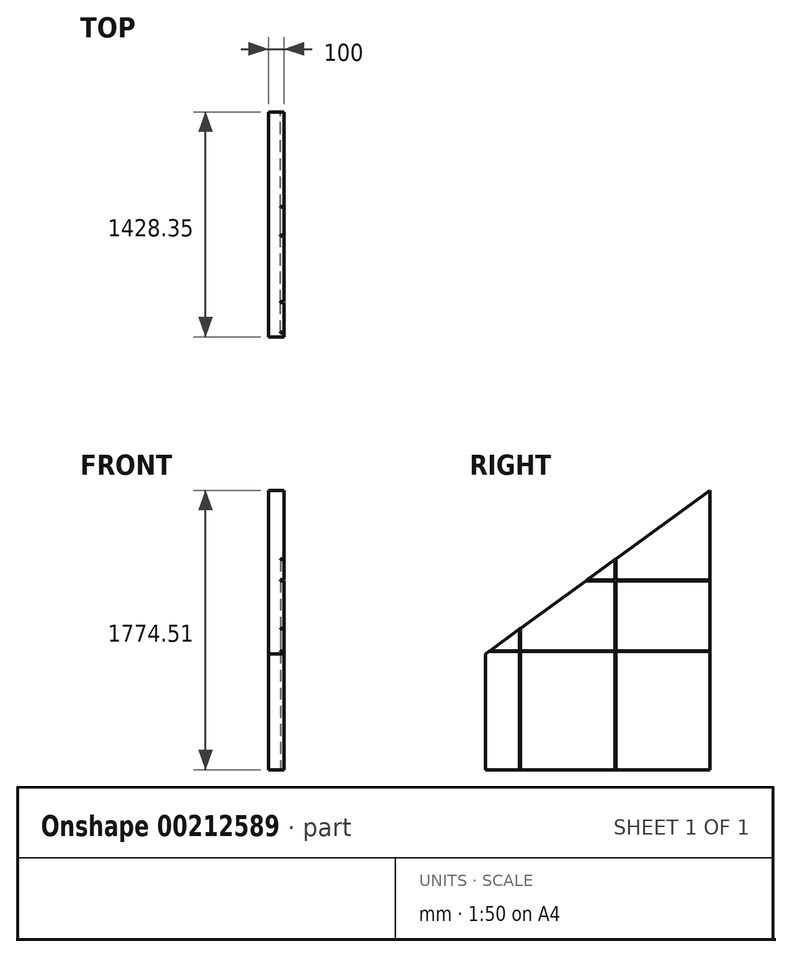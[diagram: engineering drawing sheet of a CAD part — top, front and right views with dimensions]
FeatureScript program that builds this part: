
annotation { "Feature Type Name" : "Feature", "Feature Type Description" : "" }
export const myFeature = defineFeature(function(context is Context, id is Id, definition is map)
    precondition{}
    {
        {
            var Q0;
            Q0=qCreatedBy(makeId("Right.planeOp"),FACE);
            var sketch = newSketch(context, id + "F0", { "sketchPlane" : qUnion([Q0])});
            skLineSegment(sketch, "E0", {"start": v(299.03, 33.49) * mm, "end": v(2949.03, 33.49) * mm, "construction": true});
            skLineSegment(sketch, "E1", {"start": v(2949.03, 33.49) * mm, "end": v(2949.03, 1819.49) * mm, "construction": true});
            skLineSegment(sketch, "E2", {"start": v(2949.03, 1819.49) * mm, "end": v(1899.03, 1819.49) * mm, "construction": true});
            skLineSegment(sketch, "E3", {"start": v(1899.03, 1819.49) * mm, "end": v(299.03, 653.49) * mm, "construction": true});
            skLineSegment(sketch, "E4", {"start": v(299.03, 653.49) * mm, "end": v(299.03, 33.49) * mm, "construction": true});
            skLineSegment(sketch, "E5", {"start": v(389.03, 33.49) * mm, "end": v(389.03, 767.1) * mm});
            skLineSegment(sketch, "E6", {"start": v(389.03, 767.1) * mm, "end": v(1817.38, 1808) * mm});
            skLineSegment(sketch, "E7", {"start": v(1817.38, 1808) * mm, "end": v(1817.38, 33.49) * mm});
            skLineSegment(sketch, "E8", {"start": v(1817.38, 33.49) * mm, "end": v(389.03, 33.49) * mm});
            skSolve(sketch);
        }
        {
            var Q0;
            Q0=makeQuery(id+"F0.imprint","IMPRINT",FACE,{"disambiguationData":[TD([[makeQuery(id+"F0.imprint","IMPRINT",EDGE,{"derivedFrom":sQuery(id+"F0.wireOp",EDGE,"E5")}),-1.0]])]});
            extrude(context, id + "F1", {"entities" : qUnion([Q0]), "oppositeDirection" : true, "depth" : 100 * mm});
        }
        {
            var Q0;
            Q0=qCreatedBy(makeId("Right.planeOp"),FACE);
            var sketch = newSketch(context, id + "F2", { "sketchPlane" : qUnion([Q0])});
            skLineSegment(sketch, "E9.bottom", {"start": v(1217.38, 1819.49) * mm, "end": v(1212.38, 1819.49) * mm});
            skLineSegment(sketch, "E9.top", {"start": v(1217.38, 33.49) * mm, "end": v(1212.38, 33.49) * mm});
            skLineSegment(sketch, "E9.left", {"start": v(1217.38, 1819.49) * mm, "end": v(1217.38, 33.49) * mm});
            skLineSegment(sketch, "E9.right", {"start": v(1212.38, 1819.49) * mm, "end": v(1212.38, 33.49) * mm});
            skLineSegment(sketch, "E10.bottom", {"start": v(612.38, 1819.49) * mm, "end": v(607.38, 1819.49) * mm});
            skLineSegment(sketch, "E10.top", {"start": v(612.38, 33.49) * mm, "end": v(607.38, 33.49) * mm});
            skLineSegment(sketch, "E10.left", {"start": v(612.38, 1819.49) * mm, "end": v(612.38, 33.49) * mm});
            skLineSegment(sketch, "E10.right", {"start": v(607.38, 1819.49) * mm, "end": v(607.38, 33.49) * mm});
            skLineSegment(sketch, "E11.bottom", {"start": v(0, 1238.49) * mm, "end": v(2854.16, 1238.49) * mm});
            skLineSegment(sketch, "E11.top", {"start": v(0, 1233.49) * mm, "end": v(2854.16, 1233.49) * mm});
            skLineSegment(sketch, "E11.left", {"start": v(0, 1238.49) * mm, "end": v(0, 1233.49) * mm});
            skLineSegment(sketch, "E11.right", {"start": v(2854.16, 1238.49) * mm, "end": v(2854.16, 1233.49) * mm});
            skSolve(sketch);
        }
        {
            var Q0;
            Q0 = qSketchRegion(id + "F2", true);
            extrude(context, id + "F3", {"entities" : qUnion([Q0]), "operationType" : NewBodyOperationType.REMOVE, "oppositeDirection" : true, "depth" : 25 * mm});
        }
        {
            var Q0;
            Q0=makeQuery(id+"F0.imprint","IMPRINT",FACE,{"disambiguationData":[TD([[makeQuery(id+"F0.imprint","IMPRINT",EDGE,{"derivedFrom":sQuery(id+"F0.wireOp",EDGE,"E5")}),-1.0]])]});
            var sketch = newSketch(context, id + "F4", { "sketchPlane" : qUnion([Q0])});
            skLineSegment(sketch, "E12.bottom", {"start": v(299.03, 788.49) * mm, "end": v(2949.03, 788.49) * mm});
            skLineSegment(sketch, "E12.top", {"start": v(299.03, 783.49) * mm, "end": v(2949.03, 783.49) * mm});
            skLineSegment(sketch, "E12.left", {"start": v(299.03, 788.49) * mm, "end": v(299.03, 783.49) * mm});
            skLineSegment(sketch, "E12.right", {"start": v(2949.03, 788.49) * mm, "end": v(2949.03, 783.49) * mm});
            skSolve(sketch);
        }
        {
            var Q0;
            Q0 = qSketchRegion(id + "F4", true);
            extrude(context, id + "F5", {"entities" : qUnion([Q0]), "operationType" : NewBodyOperationType.REMOVE, "oppositeDirection" : true, "depth" : 25 * mm});
        }
    });
